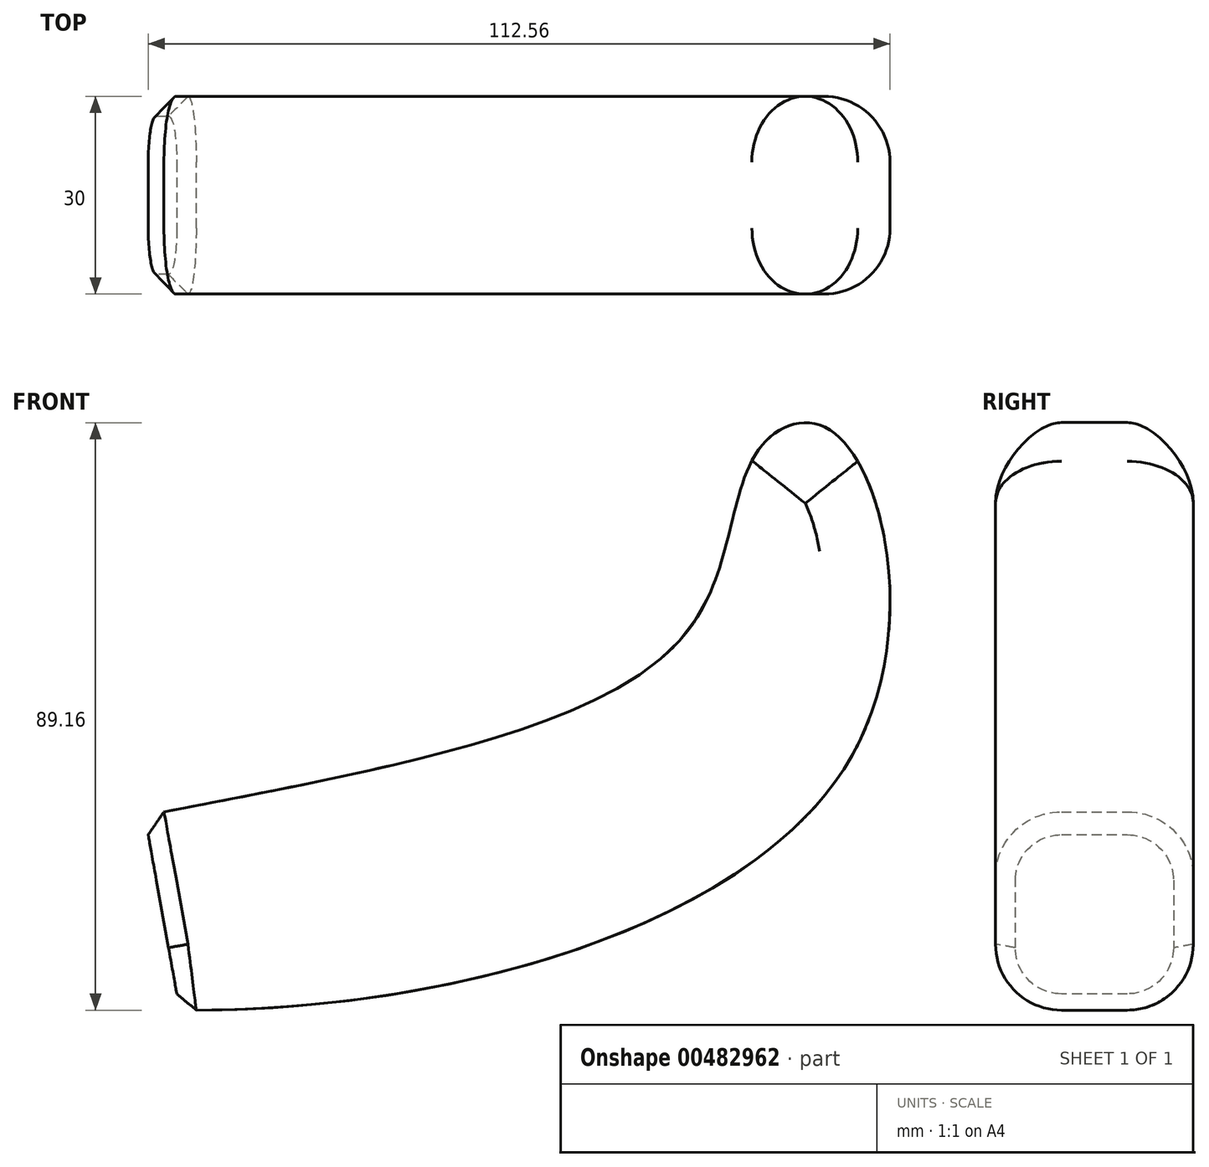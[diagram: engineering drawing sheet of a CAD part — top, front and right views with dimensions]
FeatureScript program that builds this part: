
annotation { "Feature Type Name" : "Feature", "Feature Type Description" : "" }
export const myFeature = defineFeature(function(context is Context, id is Id, definition is map)
    precondition{}
    {
        {
            var Q0;
            Q0=qCreatedBy(makeId("Front.planeOp"),FACE);
            var sketch = newSketch(context, id + "F0", { "sketchPlane" : qUnion([Q0])});
            skFitSpline(sketch, "E0", {"points": [v(-39, -102.54) * mm, v(44.06, -73.6) * mm, v(53.94, -47.32) * mm, v(65.31, -44.28) * mm, v(68.18, -93.66) * mm, v(-41.32, -131.8) * mm, v(-96.44, -124.96) * mm], "startDerivative": vector(575.22, 109.52) * mm, "endDerivative": vector(-101.14, -61.45) * mm});
            skLineSegment(sketch, "E1", {"start": v(-39, -102.54) * mm, "end": v(-33.7, -132.07) * mm});
            skLineSegment(sketch, "E2", {"start": v(62.34, 0) * mm, "end": v(94, -176.13) * mm});
            skLineSegment(sketch, "E3", {"start": v(70.4, -202.52) * mm, "end": v(34, 0) * mm});
            skSolve(sketch);
        }
        {
            var Q0;
            Q0=makeQuery(id+"F0.imprint","IMPRINT",FACE,{"disambiguationData":[TD([[makeQuery(id+"F0.imprint","IMPRINT",EDGE,{"derivedFrom":sQuery(id+"F0.wireOp",EDGE,"E0")}),-1.0]])]});
            var Q1;
            {var subQ0=sQuery(id+"F0.wireOp",EDGE,"E3");var subQ1=sQuery(id+"F0.wireOp",EDGE,"E0");var subQ2=makeQuery(id+"F0.imprint","INTERSECT",VERTEX,{"disambiguationData":[OD(0.0)],"derivedFrom":[subQ1,subQ0]});Q1=makeQuery(id+"F0.imprint","IMPRINT",FACE,{"disambiguationData":[TD([[makeQuery(id+"F0.imprint","IMPRINT",EDGE,{"disambiguationData":[TD([[subQ2,-1.0]])],"derivedFrom":subQ1}),-1.0]])]});}
            extrude(context, id + "F1", {"entities" : qUnion([Q0, Q1]), "depth" : 30 * mm, "offsetDistance" : 25 * mm});
        }
        {
            var Q0;
            Q0=makeQuery(id+"F1.opExtrude","CAP_EDGE",EDGE,{"disambiguationData":[OSD([sQuery(id+"F0.wireOp",EDGE,"E0")])],"isStart":false});
            var Q1;
            Q1=makeQuery(id+"F1.opExtrude","CAP_EDGE",EDGE,{"disambiguationData":[OSD([sQuery(id+"F0.wireOp",EDGE,"E0")])],"isStart":true});
            fillet(context, id + "F2", {"entities" : qUnion([Q0, Q1]), "radius" : 10 * mm, "tangentPropagation" : true, "allowEdgeOverflow" : false});
        }
        {
            var Q0;
            {var subQ0=sQuery(id+"F0.wireOp",EDGE,"E1");var subQ1=sQuery(id+"F0.wireOp",EDGE,"E0");Q0=makeQuery(id+"F1.opExtrude","SWEPT_EDGE",EDGE,{"disambiguationData":[OSD([subQ1,subQ0]),TDD([makeQuery(id+"F0.imprint","INTERSECT",VERTEX,{"disambiguationData":[OD(0.0)],"derivedFrom":[subQ1,subQ0]})])]});}
            var Q1;
            Q1=makeQuery(id+"F2.opFillet","BLEND_EDGE",EDGE,{"disambiguationData":[OD(0.0)],"blendedFrom":[makeQuery(id+"F1.opExtrude","CAP_EDGE",EDGE,{"disambiguationData":[OSD([sQuery(id+"F0.wireOp",EDGE,"E0")])],"isStart":true}),makeQuery(id+"F1.opExtrude","SWEPT_FACE",FACE,{"disambiguationData":[OSD([sQuery(id+"F0.wireOp",EDGE,"E1")])]})],"blendedInto":[makeQuery(id+"F1.opExtrude","SWEPT_FACE",FACE,{"disambiguationData":[OSD([sQuery(id+"F0.wireOp",EDGE,"E1")])]})]});
            var Q2;
            Q2=makeQuery(id+"F2.opFillet","BLEND_EDGE",EDGE,{"disambiguationData":[OD(0.0)],"blendedFrom":[makeQuery(id+"F1.opExtrude","CAP_EDGE",EDGE,{"disambiguationData":[OSD([sQuery(id+"F0.wireOp",EDGE,"E0")])],"isStart":false}),makeQuery(id+"F1.opExtrude","SWEPT_FACE",FACE,{"disambiguationData":[OSD([sQuery(id+"F0.wireOp",EDGE,"E1")])]})],"blendedInto":[makeQuery(id+"F1.opExtrude","SWEPT_FACE",FACE,{"disambiguationData":[OSD([sQuery(id+"F0.wireOp",EDGE,"E1")])]})]});
            var Q3;
            Q3=makeQuery(id+"F2.opFillet","BLEND_EDGE",EDGE,{"disambiguationData":[OD(1.0)],"blendedFrom":[makeQuery(id+"F1.opExtrude","CAP_EDGE",EDGE,{"disambiguationData":[OSD([sQuery(id+"F0.wireOp",EDGE,"E0")])],"isStart":false}),makeQuery(id+"F1.opExtrude","SWEPT_FACE",FACE,{"disambiguationData":[OSD([sQuery(id+"F0.wireOp",EDGE,"E1")])]})],"blendedInto":[makeQuery(id+"F1.opExtrude","SWEPT_FACE",FACE,{"disambiguationData":[OSD([sQuery(id+"F0.wireOp",EDGE,"E1")])]})]});
            var Q4;
            Q4=makeQuery(id+"F1.opExtrude","CAP_EDGE",EDGE,{"disambiguationData":[OSD([sQuery(id+"F0.wireOp",EDGE,"E1")])],"isStart":false});
            var Q5;
            {var subQ0=sQuery(id+"F0.wireOp",EDGE,"E1");var subQ1=sQuery(id+"F0.wireOp",EDGE,"E0");Q5=makeQuery(id+"F1.opExtrude","SWEPT_EDGE",EDGE,{"disambiguationData":[OSD([subQ1,subQ0]),TDD([makeQuery(id+"F0.imprint","INTERSECT",VERTEX,{"disambiguationData":[OD(1.0)],"derivedFrom":[subQ1,subQ0]})])]});}
            var Q6;
            Q6=makeQuery(id+"F2.opFillet","BLEND_EDGE",EDGE,{"disambiguationData":[OD(1.0)],"blendedFrom":[makeQuery(id+"F1.opExtrude","CAP_EDGE",EDGE,{"disambiguationData":[OSD([sQuery(id+"F0.wireOp",EDGE,"E0")])],"isStart":true}),makeQuery(id+"F1.opExtrude","SWEPT_FACE",FACE,{"disambiguationData":[OSD([sQuery(id+"F0.wireOp",EDGE,"E1")])]})],"blendedInto":[makeQuery(id+"F1.opExtrude","SWEPT_FACE",FACE,{"disambiguationData":[OSD([sQuery(id+"F0.wireOp",EDGE,"E1")])]})]});
            var Q7;
            Q7=makeQuery(id+"F2.opFillet","BLEND_EDGE",EDGE,{"disambiguationData":[OD(1.0)],"blendedFrom":[makeQuery(id+"F1.opExtrude","CAP_EDGE",EDGE,{"disambiguationData":[OSD([sQuery(id+"F0.wireOp",EDGE,"E0")])],"isStart":true}),makeQuery(id+"F1.opExtrude","SWEPT_FACE",FACE,{"disambiguationData":[OSD([sQuery(id+"F0.wireOp",EDGE,"E1")])]})],"blendedInto":[makeQuery(id+"F1.opExtrude","SWEPT_FACE",FACE,{"disambiguationData":[OSD([sQuery(id+"F0.wireOp",EDGE,"E1")])]})]});
            var Q8;
            Q8=makeQuery(id+"F1.opExtrude","CAP_EDGE",EDGE,{"disambiguationData":[OSD([sQuery(id+"F0.wireOp",EDGE,"E1")])],"isStart":true});
            chamfer(context, id + "F3", {"entities" : qUnion([Q0, Q1, Q2, Q3, Q4, Q5, Q6, Q7, Q8]), "width" : 3 * mm, "tangentPropagation" : true});
        }
    });
